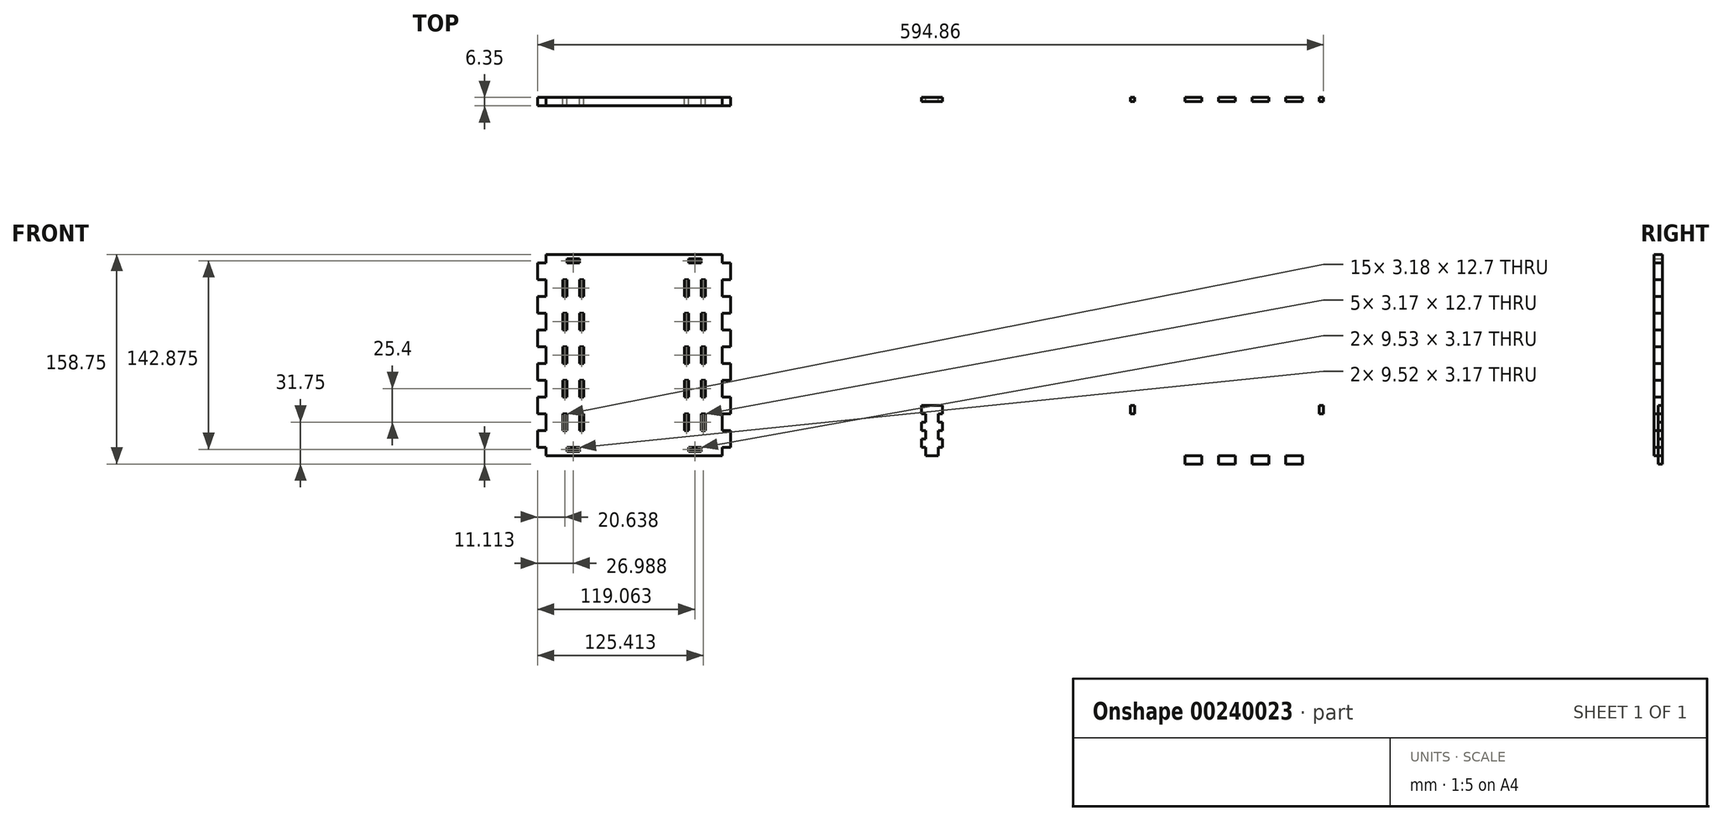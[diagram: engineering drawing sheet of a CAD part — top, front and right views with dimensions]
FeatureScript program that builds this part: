
annotation { "Feature Type Name" : "Feature", "Feature Type Description" : "" }
export const myFeature = defineFeature(function(context is Context, id is Id, definition is map)
    precondition{}
    {
        {
            var Q0;
            Q0=qCreatedBy(makeId("Front.planeOp"),FACE);
            var sketch = newSketch(context, id + "F0", { "sketchPlane" : qUnion([Q0])});
            skLineSegment(sketch, "E0.bottom", {"start": v(0, 0) * mm, "end": v(146.05, 0) * mm});
            skLineSegment(sketch, "E0.top", {"start": v(0, 38.1) * mm, "end": v(146.05, 38.1) * mm});
            skLineSegment(sketch, "E0.left", {"start": v(0, 0) * mm, "end": v(0, 38.1) * mm});
            skLineSegment(sketch, "E0.right", {"start": v(146.05, 0) * mm, "end": v(146.05, 38.1) * mm});
            skLineSegment(sketch, "E1.bottom", {"start": v(0, 38.1) * mm, "end": v(3.17, 38.1) * mm});
            skLineSegment(sketch, "E1.top", {"start": v(0, 31.75) * mm, "end": v(3.17, 31.75) * mm});
            skLineSegment(sketch, "E1.left", {"start": v(0, 38.1) * mm, "end": v(0, 31.75) * mm});
            skLineSegment(sketch, "E1.right", {"start": v(3.17, 38.1) * mm, "end": v(3.17, 31.75) * mm});
            skLineSegment(sketch, "E2.0.1.0", {"start": v(0, 19.05) * mm, "end": v(3.17, 19.05) * mm});
            skLineSegment(sketch, "E2.0.1.1", {"start": v(3.17, 25.4) * mm, "end": v(3.17, 19.05) * mm});
            skLineSegment(sketch, "E2.0.1.2", {"start": v(0, 25.4) * mm, "end": v(3.17, 25.4) * mm});
            skLineSegment(sketch, "E2.0.1.3", {"start": v(0, 25.4) * mm, "end": v(0, 19.05) * mm});
            skLineSegment(sketch, "E2.0.2.0", {"start": v(0, 6.35) * mm, "end": v(3.17, 6.35) * mm});
            skLineSegment(sketch, "E2.0.2.1", {"start": v(3.17, 12.7) * mm, "end": v(3.17, 6.35) * mm});
            skLineSegment(sketch, "E2.0.2.2", {"start": v(0, 12.7) * mm, "end": v(3.17, 12.7) * mm});
            skLineSegment(sketch, "E2.0.2.3", {"start": v(0, 12.7) * mm, "end": v(0, 6.35) * mm});
            skLineSegment(sketch, "E2.direction1", {"start": v(0, 25.4) * mm, "end": v(25.4, 25.4) * mm, "construction": true});
            skLineSegment(sketch, "E2.direction2", {"start": v(0, 25.4) * mm, "end": v(0, 12.7) * mm, "construction": true});
            skLineSegment(sketch, "E3.bottom", {"start": v(15.88, 0) * mm, "end": v(28.58, 0) * mm});
            skLineSegment(sketch, "E3.top", {"start": v(15.88, -6.35) * mm, "end": v(28.58, -6.35) * mm});
            skLineSegment(sketch, "E3.left", {"start": v(15.88, 0) * mm, "end": v(15.88, -6.35) * mm});
            skLineSegment(sketch, "E3.right", {"start": v(28.58, 0) * mm, "end": v(28.58, -6.35) * mm});
            skLineSegment(sketch, "E4.1.0.0", {"start": v(41.27, -6.35) * mm, "end": v(53.97, -6.35) * mm});
            skLineSegment(sketch, "E4.1.0.1", {"start": v(53.97, 0) * mm, "end": v(53.97, -6.35) * mm});
            skLineSegment(sketch, "E4.1.0.2", {"start": v(41.27, 0) * mm, "end": v(41.27, -6.35) * mm});
            skLineSegment(sketch, "E4.1.0.3", {"start": v(41.27, 0) * mm, "end": v(53.97, 0) * mm});
            skLineSegment(sketch, "E4.2.0.0", {"start": v(66.67, -6.35) * mm, "end": v(79.37, -6.35) * mm});
            skLineSegment(sketch, "E4.2.0.1", {"start": v(79.37, 0) * mm, "end": v(79.37, -6.35) * mm});
            skLineSegment(sketch, "E4.2.0.2", {"start": v(66.67, 0) * mm, "end": v(66.67, -6.35) * mm});
            skLineSegment(sketch, "E4.2.0.3", {"start": v(66.67, 0) * mm, "end": v(79.37, 0) * mm});
            skLineSegment(sketch, "E4.3.0.0", {"start": v(92.07, -6.35) * mm, "end": v(104.77, -6.35) * mm});
            skLineSegment(sketch, "E4.3.0.1", {"start": v(104.77, 0) * mm, "end": v(104.77, -6.35) * mm});
            skLineSegment(sketch, "E4.3.0.2", {"start": v(92.07, 0) * mm, "end": v(92.07, -6.35) * mm});
            skLineSegment(sketch, "E4.3.0.3", {"start": v(92.07, 0) * mm, "end": v(104.77, 0) * mm});
            skLineSegment(sketch, "E4.4.0.0", {"start": v(117.47, -6.35) * mm, "end": v(130.17, -6.35) * mm});
            skLineSegment(sketch, "E4.4.0.1", {"start": v(130.17, 0) * mm, "end": v(130.17, -6.35) * mm});
            skLineSegment(sketch, "E4.4.0.2", {"start": v(117.47, 0) * mm, "end": v(117.47, -6.35) * mm});
            skLineSegment(sketch, "E4.4.0.3", {"start": v(117.47, 0) * mm, "end": v(130.17, 0) * mm});
            skLineSegment(sketch, "E4.direction1", {"start": v(3.18, -3.18) * mm, "end": v(28.58, -3.18) * mm, "construction": true});
            skLineSegment(sketch, "E5", {"start": v(73.03, 38.1) * mm, "end": v(73.03, 0) * mm, "construction": true});
            skLineSegment(sketch, "E6.MirrorCS", {"start": v(146.05, 12.7) * mm, "end": v(142.88, 12.7) * mm});
            skLineSegment(sketch, "E7.MirrorCS", {"start": v(146.05, 31.75) * mm, "end": v(142.88, 31.75) * mm});
            skLineSegment(sketch, "E8.MirrorCS", {"start": v(146.05, 19.05) * mm, "end": v(142.88, 19.05) * mm});
            skLineSegment(sketch, "E9.MirrorCS", {"start": v(146.05, 25.4) * mm, "end": v(142.88, 25.4) * mm});
            skLineSegment(sketch, "E10.MirrorCS", {"start": v(146.05, 6.35) * mm, "end": v(142.88, 6.35) * mm});
            skLineSegment(sketch, "E11.MirrorCS", {"start": v(142.88, 12.7) * mm, "end": v(142.88, 6.35) * mm});
            skLineSegment(sketch, "E12.MirrorCS", {"start": v(142.88, 38.1) * mm, "end": v(142.88, 31.75) * mm});
            skLineSegment(sketch, "E13.MirrorCS", {"start": v(142.88, 25.4) * mm, "end": v(142.88, 19.05) * mm});
            skLineSegment(sketch, "E14.MirrorCS", {"start": v(146.05, 25.4) * mm, "end": v(120.65, 25.4) * mm, "construction": true});
            skLineSegment(sketch, "E15.MirrorCS", {"start": v(146.05, 38.1) * mm, "end": v(142.88, 38.1) * mm});
            skLineSegment(sketch, "E16.MirrorCS", {"start": v(146.05, 38.1) * mm, "end": v(146.05, 31.75) * mm});
            skLineSegment(sketch, "E17.MirrorCS", {"start": v(146.05, 25.4) * mm, "end": v(146.05, 12.7) * mm, "construction": true});
            skSolve(sketch);
        }
        {
            var Q0;
            Q0=makeQuery(id+"F0.imprint","IMPRINT",FACE,{"disambiguationData":[TD([[makeQuery(id+"F0.imprint","IMPRINT",EDGE,{"derivedFrom":sQuery(id+"F0.wireOp",EDGE,"E0.top")}),-1.0]])]});
            var Q1;
            Q1=makeQuery(id+"F0.imprint","IMPRINT",FACE,{"disambiguationData":[TD([[makeQuery(id+"F0.imprint","IMPRINT",EDGE,{"derivedFrom":sQuery(id+"F0.wireOp",EDGE,"E3.bottom")}),-1.0]])]});
            var Q2;
            Q2=makeQuery(id+"F0.imprint","IMPRINT",FACE,{"disambiguationData":[TD([[makeQuery(id+"F0.imprint","IMPRINT",EDGE,{"derivedFrom":sQuery(id+"F0.wireOp",EDGE,"E4.1.0.0")}),1.0]])]});
            var Q3;
            Q3=makeQuery(id+"F0.imprint","IMPRINT",FACE,{"disambiguationData":[TD([[makeQuery(id+"F0.imprint","IMPRINT",EDGE,{"derivedFrom":sQuery(id+"F0.wireOp",EDGE,"E4.2.0.0")}),1.0]])]});
            var Q4;
            Q4=makeQuery(id+"F0.imprint","IMPRINT",FACE,{"disambiguationData":[TD([[makeQuery(id+"F0.imprint","IMPRINT",EDGE,{"derivedFrom":sQuery(id+"F0.wireOp",EDGE,"E4.3.0.0")}),1.0]])]});
            var Q5;
            Q5=makeQuery(id+"F0.imprint","IMPRINT",FACE,{"disambiguationData":[TD([[makeQuery(id+"F0.imprint","IMPRINT",EDGE,{"derivedFrom":sQuery(id+"F0.wireOp",EDGE,"E4.4.0.0")}),1.0]])]});
            extrude(context, id + "F1", {"entities" : qUnion([Q0, Q1, Q2, Q3, Q4, Q5]), "depth" : 3.17 * mm});
        }
        {
            var Q0;
            Q0=qCreatedBy(makeId("Front.planeOp"),FACE);
            var sketch = newSketch(context, id + "F2", { "sketchPlane" : qUnion([Q0])});
            skLineSegment(sketch, "E18.bottom", {"start": v(-145.64, 0) * mm, "end": v(-155.16, 0) * mm});
            skLineSegment(sketch, "E18.top", {"start": v(-145.64, 38.1) * mm, "end": v(-155.16, 38.1) * mm});
            skLineSegment(sketch, "E18.left", {"start": v(-145.64, 0) * mm, "end": v(-145.64, 38.1) * mm});
            skLineSegment(sketch, "E18.right", {"start": v(-155.16, 0) * mm, "end": v(-155.16, 38.1) * mm});
            skLineSegment(sketch, "E19.bottom", {"start": v(-145.64, 38.1) * mm, "end": v(-142.46, 38.1) * mm});
            skLineSegment(sketch, "E19.top", {"start": v(-145.64, 31.75) * mm, "end": v(-142.46, 31.75) * mm});
            skLineSegment(sketch, "E19.left", {"start": v(-145.64, 38.1) * mm, "end": v(-145.64, 31.75) * mm});
            skLineSegment(sketch, "E19.right", {"start": v(-142.46, 38.1) * mm, "end": v(-142.46, 31.75) * mm});
            skLineSegment(sketch, "E20.0.1.0", {"start": v(-142.46, 25.4) * mm, "end": v(-142.46, 19.05) * mm});
            skLineSegment(sketch, "E20.0.1.1", {"start": v(-145.64, 25.4) * mm, "end": v(-142.46, 25.4) * mm});
            skLineSegment(sketch, "E20.0.1.2", {"start": v(-145.64, 19.05) * mm, "end": v(-142.46, 19.05) * mm});
            skLineSegment(sketch, "E20.0.1.3", {"start": v(-155.16, -12.7) * mm, "end": v(-155.16, 25.4) * mm});
            skLineSegment(sketch, "E20.0.2.0", {"start": v(-142.46, 12.7) * mm, "end": v(-142.46, 6.35) * mm});
            skLineSegment(sketch, "E20.0.2.1", {"start": v(-145.64, 12.7) * mm, "end": v(-142.46, 12.7) * mm});
            skLineSegment(sketch, "E20.0.2.2", {"start": v(-145.64, 6.35) * mm, "end": v(-142.46, 6.35) * mm});
            skLineSegment(sketch, "E20.0.2.3", {"start": v(-155.16, -25.4) * mm, "end": v(-155.16, 12.7) * mm});
            skLineSegment(sketch, "E20.direction1", {"start": v(-145.64, 31.75) * mm, "end": v(-122.14, 31.75) * mm, "construction": true});
            skLineSegment(sketch, "E20.direction2", {"start": v(-145.64, 31.75) * mm, "end": v(-145.64, 19.05) * mm, "construction": true});
            skLineSegment(sketch, "E21", {"start": v(-150.4, 38.1) * mm, "end": v(-150.4, 0) * mm, "construction": true});
            skLineSegment(sketch, "E22.MirrorCS", {"start": v(-155.16, 25.4) * mm, "end": v(-158.34, 25.4) * mm});
            skLineSegment(sketch, "E23.MirrorCS", {"start": v(-155.16, 19.05) * mm, "end": v(-158.34, 19.05) * mm});
            skLineSegment(sketch, "E24.MirrorCS", {"start": v(-155.16, 31.75) * mm, "end": v(-158.34, 31.75) * mm});
            skLineSegment(sketch, "E25.MirrorCS", {"start": v(-155.16, 38.1) * mm, "end": v(-158.34, 38.1) * mm});
            skLineSegment(sketch, "E26.MirrorCS", {"start": v(-155.16, 12.7) * mm, "end": v(-158.34, 12.7) * mm});
            skLineSegment(sketch, "E27.MirrorCS", {"start": v(-155.16, 6.35) * mm, "end": v(-158.34, 6.35) * mm});
            skLineSegment(sketch, "E28.MirrorCS", {"start": v(-158.34, 38.1) * mm, "end": v(-158.34, 31.75) * mm});
            skLineSegment(sketch, "E29.MirrorCS", {"start": v(-158.34, 25.4) * mm, "end": v(-158.34, 19.05) * mm});
            skLineSegment(sketch, "E30.MirrorCS", {"start": v(-158.34, 12.7) * mm, "end": v(-158.34, 6.35) * mm});
            skLineSegment(sketch, "E31.MirrorCS", {"start": v(-155.16, 31.75) * mm, "end": v(-178.66, 31.75) * mm, "construction": true});
            skLineSegment(sketch, "E32.bottom", {"start": v(-155.16, 0) * mm, "end": v(-145.64, 0) * mm});
            skLineSegment(sketch, "E32.top", {"start": v(-155.16, -6.35) * mm, "end": v(-145.64, -6.35) * mm});
            skLineSegment(sketch, "E32.left", {"start": v(-155.16, 0) * mm, "end": v(-155.16, -6.35) * mm});
            skLineSegment(sketch, "E32.right", {"start": v(-145.64, 0) * mm, "end": v(-145.64, -6.35) * mm});
            skSolve(sketch);
        }
        {
            var Q0;
            {var subQ7=sQuery(id+"F2.wireOp",EDGE,"E18.top");Q0=makeQuery(id+"F2.imprint","IMPRINT",FACE,{"disambiguationData":[TD([[makeQuery(id+"F2.imprint","IMPRINT",EDGE,{"derivedFrom":subQ7}),1.0]])]});}
            var Q1;
            {var subQ0=sQuery(id+"F2.wireOp",EDGE,"E22.MirrorCS");Q1=makeQuery(id+"F2.imprint","IMPRINT",FACE,{"disambiguationData":[TD([[makeQuery(id+"F2.imprint","IMPRINT",EDGE,{"derivedFrom":subQ0}),1.0]])]});}
            var Q2;
            {var subQ0=sQuery(id+"F2.wireOp",EDGE,"E26.MirrorCS");Q2=makeQuery(id+"F2.imprint","IMPRINT",FACE,{"disambiguationData":[TD([[makeQuery(id+"F2.imprint","IMPRINT",EDGE,{"derivedFrom":subQ0}),1.0]])]});}
            var Q3;
            Q3=makeQuery(id+"F2.imprint","IMPRINT",FACE,{"disambiguationData":[TD([[makeQuery(id+"F2.imprint","IMPRINT",EDGE,{"derivedFrom":sQuery(id+"F2.wireOp",EDGE,"E20.0.2.0")}),-1.0]])]});
            var Q4;
            Q4=makeQuery(id+"F2.imprint","IMPRINT",FACE,{"disambiguationData":[TD([[makeQuery(id+"F2.imprint","IMPRINT",EDGE,{"derivedFrom":sQuery(id+"F2.wireOp",EDGE,"E20.0.1.0")}),-1.0]])]});
            var Q5;
            Q5=makeQuery(id+"F2.imprint","IMPRINT",FACE,{"disambiguationData":[TD([[makeQuery(id+"F2.imprint","IMPRINT",EDGE,{"derivedFrom":sQuery(id+"F2.wireOp",EDGE,"E19.bottom")}),-1.0]])]});
            var Q6;
            {var subQ2=sQuery(id+"F2.wireOp",EDGE,"E24.MirrorCS");Q6=makeQuery(id+"F2.imprint","IMPRINT",FACE,{"disambiguationData":[TD([[makeQuery(id+"F2.imprint","IMPRINT",EDGE,{"derivedFrom":subQ2}),-1.0]])]});}
            var Q7;
            Q7=makeQuery(id+"F2.imprint","IMPRINT",FACE,{"disambiguationData":[TD([[makeQuery(id+"F2.imprint","IMPRINT",EDGE,{"derivedFrom":sQuery(id+"F2.wireOp",EDGE,"E32.bottom")}),-1.0]])]});
            extrude(context, id + "F3", {"entities" : qUnion([Q0, Q1, Q2, Q3, Q4, Q5, Q6, Q7]), "depth" : 3.17 * mm});
        }
        {
            var Q0;
            Q0=qCreatedBy(makeId("Front.planeOp"),FACE);
            var sketch = newSketch(context, id + "F4", { "sketchPlane" : qUnion([Q0])});
            skLineSegment(sketch, "E33.bottom", {"start": v(-309.1, 0) * mm, "end": v(-442.46, 0) * mm});
            skLineSegment(sketch, "E33.top", {"start": v(-309.1, 152.4) * mm, "end": v(-442.46, 152.4) * mm});
            skLineSegment(sketch, "E33.left", {"start": v(-309.1, 0) * mm, "end": v(-309.1, 152.4) * mm});
            skLineSegment(sketch, "E33.right", {"start": v(-442.46, 0) * mm, "end": v(-442.46, 152.4) * mm});
            skLineSegment(sketch, "E34.bottom", {"start": v(-309.1, 146.05) * mm, "end": v(-302.76, 146.05) * mm});
            skLineSegment(sketch, "E34.top", {"start": v(-309.1, 133.35) * mm, "end": v(-302.76, 133.35) * mm});
            skLineSegment(sketch, "E34.left", {"start": v(-309.1, 146.05) * mm, "end": v(-309.1, 133.35) * mm});
            skLineSegment(sketch, "E34.right", {"start": v(-302.76, 146.05) * mm, "end": v(-302.76, 133.35) * mm});
            skLineSegment(sketch, "E35.0.1.0", {"start": v(-309.1, 107.95) * mm, "end": v(-302.76, 107.95) * mm});
            skLineSegment(sketch, "E35.0.1.1", {"start": v(-309.1, 120.65) * mm, "end": v(-302.76, 120.65) * mm});
            skLineSegment(sketch, "E35.0.1.2", {"start": v(-302.76, 120.65) * mm, "end": v(-302.76, 107.95) * mm});
            skLineSegment(sketch, "E35.0.2.0", {"start": v(-309.1, 82.55) * mm, "end": v(-302.76, 82.55) * mm});
            skLineSegment(sketch, "E35.0.2.1", {"start": v(-309.1, 95.25) * mm, "end": v(-302.76, 95.25) * mm});
            skLineSegment(sketch, "E35.0.2.2", {"start": v(-302.76, 95.25) * mm, "end": v(-302.76, 82.55) * mm});
            skLineSegment(sketch, "E35.0.3.0", {"start": v(-309.1, 57.15) * mm, "end": v(-302.76, 57.15) * mm});
            skLineSegment(sketch, "E35.0.3.1", {"start": v(-309.1, 69.85) * mm, "end": v(-302.76, 69.85) * mm});
            skLineSegment(sketch, "E35.0.3.2", {"start": v(-302.76, 69.85) * mm, "end": v(-302.76, 57.15) * mm});
            skLineSegment(sketch, "E35.0.4.0", {"start": v(-309.1, 31.75) * mm, "end": v(-302.76, 31.75) * mm});
            skLineSegment(sketch, "E35.0.4.1", {"start": v(-309.1, 44.45) * mm, "end": v(-302.76, 44.45) * mm});
            skLineSegment(sketch, "E35.0.4.2", {"start": v(-302.76, 44.45) * mm, "end": v(-302.76, 31.75) * mm});
            skLineSegment(sketch, "E35.0.5.0", {"start": v(-309.1, 6.35) * mm, "end": v(-302.76, 6.35) * mm});
            skLineSegment(sketch, "E35.0.5.1", {"start": v(-309.1, 19.05) * mm, "end": v(-302.76, 19.05) * mm});
            skLineSegment(sketch, "E35.0.5.2", {"start": v(-302.76, 19.05) * mm, "end": v(-302.76, 6.35) * mm});
            skLineSegment(sketch, "E35.direction1", {"start": v(-309.1, 133.35) * mm, "end": v(-283.7, 133.35) * mm, "construction": true});
            skLineSegment(sketch, "E35.direction2", {"start": v(-309.1, 133.35) * mm, "end": v(-309.1, 107.95) * mm, "construction": true});
            skLineSegment(sketch, "E36", {"start": v(-375.78, 152.4) * mm, "end": v(-375.78, 0) * mm, "construction": true});
            skLineSegment(sketch, "E37.MirrorCS", {"start": v(-442.46, 31.75) * mm, "end": v(-448.8, 31.75) * mm});
            skLineSegment(sketch, "E38.MirrorCS", {"start": v(-442.46, 57.15) * mm, "end": v(-448.8, 57.15) * mm});
            skLineSegment(sketch, "E39.MirrorCS", {"start": v(-442.46, 69.85) * mm, "end": v(-448.8, 69.85) * mm});
            skLineSegment(sketch, "E40.MirrorCS", {"start": v(-442.46, 146.05) * mm, "end": v(-448.8, 146.05) * mm});
            skLineSegment(sketch, "E41.MirrorCS", {"start": v(-442.46, 133.35) * mm, "end": v(-448.8, 133.35) * mm});
            skLineSegment(sketch, "E42.MirrorCS", {"start": v(-442.46, 107.95) * mm, "end": v(-448.8, 107.95) * mm});
            skLineSegment(sketch, "E43.MirrorCS", {"start": v(-442.46, 120.65) * mm, "end": v(-448.8, 120.65) * mm});
            skLineSegment(sketch, "E44.MirrorCS", {"start": v(-442.46, 6.35) * mm, "end": v(-448.8, 6.35) * mm});
            skLineSegment(sketch, "E45.MirrorCS", {"start": v(-442.46, 19.05) * mm, "end": v(-448.8, 19.05) * mm});
            skLineSegment(sketch, "E46.MirrorCS", {"start": v(-442.46, 82.55) * mm, "end": v(-448.8, 82.55) * mm});
            skLineSegment(sketch, "E47.MirrorCS", {"start": v(-442.46, 44.45) * mm, "end": v(-448.8, 44.45) * mm});
            skLineSegment(sketch, "E48.MirrorCS", {"start": v(-442.46, 95.25) * mm, "end": v(-448.8, 95.25) * mm});
            skLineSegment(sketch, "E49.MirrorCS", {"start": v(-448.8, 95.25) * mm, "end": v(-448.8, 82.55) * mm});
            skLineSegment(sketch, "E50.MirrorCS", {"start": v(-448.8, 69.85) * mm, "end": v(-448.8, 57.15) * mm});
            skLineSegment(sketch, "E51.MirrorCS", {"start": v(-442.46, 133.35) * mm, "end": v(-467.86, 133.35) * mm, "construction": true});
            skLineSegment(sketch, "E52.MirrorCS", {"start": v(-448.8, 146.05) * mm, "end": v(-448.8, 133.35) * mm});
            skLineSegment(sketch, "E53.MirrorCS", {"start": v(-448.8, 19.05) * mm, "end": v(-448.8, 6.35) * mm});
            skLineSegment(sketch, "E54.MirrorCS", {"start": v(-448.8, 120.65) * mm, "end": v(-448.8, 107.95) * mm});
            skLineSegment(sketch, "E55.MirrorCS", {"start": v(-448.8, 44.45) * mm, "end": v(-448.8, 31.75) * mm});
            skLineSegment(sketch, "E56.bottom", {"start": v(-429.76, 133.35) * mm, "end": v(-426.58, 133.35) * mm});
            skLineSegment(sketch, "E56.top", {"start": v(-429.76, 120.65) * mm, "end": v(-426.58, 120.65) * mm});
            skLineSegment(sketch, "E56.left", {"start": v(-429.76, 133.35) * mm, "end": v(-429.76, 120.65) * mm});
            skLineSegment(sketch, "E56.right", {"start": v(-426.58, 133.35) * mm, "end": v(-426.58, 120.65) * mm});
            skLineSegment(sketch, "E57.0.1.0", {"start": v(-426.58, 107.95) * mm, "end": v(-426.58, 95.25) * mm});
            skLineSegment(sketch, "E57.0.1.1", {"start": v(-429.76, 107.95) * mm, "end": v(-429.76, 95.25) * mm});
            skLineSegment(sketch, "E57.0.1.2", {"start": v(-429.76, 107.95) * mm, "end": v(-426.58, 107.95) * mm});
            skLineSegment(sketch, "E57.0.1.3", {"start": v(-429.76, 95.25) * mm, "end": v(-426.58, 95.25) * mm});
            skLineSegment(sketch, "E57.0.1.4", {"start": v(-442.46, -25.4) * mm, "end": v(-442.46, 127) * mm});
            skLineSegment(sketch, "E57.0.2.0", {"start": v(-426.58, 82.55) * mm, "end": v(-426.58, 69.85) * mm});
            skLineSegment(sketch, "E57.0.2.1", {"start": v(-429.76, 82.55) * mm, "end": v(-429.76, 69.85) * mm});
            skLineSegment(sketch, "E57.0.2.2", {"start": v(-429.76, 82.55) * mm, "end": v(-426.58, 82.55) * mm});
            skLineSegment(sketch, "E57.0.2.3", {"start": v(-429.76, 69.85) * mm, "end": v(-426.58, 69.85) * mm});
            skLineSegment(sketch, "E57.0.2.4", {"start": v(-442.46, -50.8) * mm, "end": v(-442.46, 101.6) * mm});
            skLineSegment(sketch, "E57.0.3.0", {"start": v(-426.58, 57.15) * mm, "end": v(-426.58, 44.45) * mm});
            skLineSegment(sketch, "E57.0.3.1", {"start": v(-429.76, 57.15) * mm, "end": v(-429.76, 44.45) * mm});
            skLineSegment(sketch, "E57.0.3.2", {"start": v(-429.76, 57.15) * mm, "end": v(-426.58, 57.15) * mm});
            skLineSegment(sketch, "E57.0.3.3", {"start": v(-429.76, 44.45) * mm, "end": v(-426.58, 44.45) * mm});
            skLineSegment(sketch, "E57.0.3.4", {"start": v(-442.46, -76.2) * mm, "end": v(-442.46, 76.2) * mm});
            skLineSegment(sketch, "E57.0.4.0", {"start": v(-426.58, 31.75) * mm, "end": v(-426.58, 19.05) * mm});
            skLineSegment(sketch, "E57.0.4.1", {"start": v(-429.76, 31.75) * mm, "end": v(-429.76, 19.05) * mm});
            skLineSegment(sketch, "E57.0.4.2", {"start": v(-429.76, 31.75) * mm, "end": v(-426.58, 31.75) * mm});
            skLineSegment(sketch, "E57.0.4.3", {"start": v(-429.76, 19.05) * mm, "end": v(-426.58, 19.05) * mm});
            skLineSegment(sketch, "E57.0.4.4", {"start": v(-442.46, -101.6) * mm, "end": v(-442.46, 50.8) * mm});
            skLineSegment(sketch, "E57.direction1", {"start": v(-429.76, 120.65) * mm, "end": v(-404.36, 120.65) * mm, "construction": true});
            skLineSegment(sketch, "E57.direction2", {"start": v(-429.76, 120.65) * mm, "end": v(-429.76, 95.25) * mm, "construction": true});
            skLineSegment(sketch, "E58", {"start": v(-421.82, 152.4) * mm, "end": v(-421.82, 0) * mm, "construction": true});
            skLineSegment(sketch, "E59.MirrorCS", {"start": v(-413.88, 107.95) * mm, "end": v(-413.88, 95.25) * mm});
            skLineSegment(sketch, "E60.MirrorCS", {"start": v(-413.88, 133.35) * mm, "end": v(-413.88, 120.65) * mm});
            skLineSegment(sketch, "E61.MirrorCS", {"start": v(-417.06, 133.35) * mm, "end": v(-417.06, 120.65) * mm});
            skLineSegment(sketch, "E62.MirrorCS", {"start": v(-413.88, 82.55) * mm, "end": v(-413.88, 69.85) * mm});
            skLineSegment(sketch, "E63.MirrorCS", {"start": v(-413.88, 82.55) * mm, "end": v(-417.06, 82.55) * mm});
            skLineSegment(sketch, "E64.MirrorCS", {"start": v(-417.06, 107.95) * mm, "end": v(-417.06, 95.25) * mm});
            skLineSegment(sketch, "E65.MirrorCS", {"start": v(-413.88, 69.85) * mm, "end": v(-417.06, 69.85) * mm});
            skLineSegment(sketch, "E66.MirrorCS", {"start": v(-413.88, 95.25) * mm, "end": v(-417.06, 95.25) * mm});
            skLineSegment(sketch, "E67.MirrorCS", {"start": v(-417.06, 57.15) * mm, "end": v(-417.06, 44.45) * mm});
            skLineSegment(sketch, "E68.MirrorCS", {"start": v(-413.88, 133.35) * mm, "end": v(-417.06, 133.35) * mm});
            skLineSegment(sketch, "E69.MirrorCS", {"start": v(-417.06, 82.55) * mm, "end": v(-417.06, 69.85) * mm});
            skLineSegment(sketch, "E70.MirrorCS", {"start": v(-413.88, 120.65) * mm, "end": v(-417.06, 120.65) * mm});
            skLineSegment(sketch, "E71.MirrorCS", {"start": v(-413.88, 57.15) * mm, "end": v(-417.06, 57.15) * mm});
            skLineSegment(sketch, "E72.MirrorCS", {"start": v(-413.88, 120.65) * mm, "end": v(-413.88, 95.25) * mm, "construction": true});
            skLineSegment(sketch, "E73.MirrorCS", {"start": v(-413.88, 107.95) * mm, "end": v(-417.06, 107.95) * mm});
            skLineSegment(sketch, "E74.MirrorCS", {"start": v(-413.88, 44.45) * mm, "end": v(-417.06, 44.45) * mm});
            skLineSegment(sketch, "E75.MirrorCS", {"start": v(-413.88, 57.15) * mm, "end": v(-413.88, 44.45) * mm});
            skLineSegment(sketch, "E76.MirrorCS", {"start": v(-413.88, 19.05) * mm, "end": v(-417.06, 19.05) * mm});
            skLineSegment(sketch, "E77.MirrorCS", {"start": v(-413.88, 31.75) * mm, "end": v(-417.06, 31.75) * mm});
            skLineSegment(sketch, "E78.MirrorCS", {"start": v(-413.88, 31.75) * mm, "end": v(-413.88, 19.05) * mm});
            skLineSegment(sketch, "E79.MirrorCS", {"start": v(-417.06, 31.75) * mm, "end": v(-417.06, 19.05) * mm});
            skLineSegment(sketch, "E80.MirrorCS", {"start": v(-337.68, 120.65) * mm, "end": v(-334.5, 120.65) * mm});
            skLineSegment(sketch, "E81.MirrorCS", {"start": v(-337.68, 95.25) * mm, "end": v(-334.5, 95.25) * mm});
            skLineSegment(sketch, "E82.MirrorCS", {"start": v(-321.8, 133.35) * mm, "end": v(-324.98, 133.35) * mm});
            skLineSegment(sketch, "E83.MirrorCS", {"start": v(-321.8, 95.25) * mm, "end": v(-324.98, 95.25) * mm});
            skLineSegment(sketch, "E84.MirrorCS", {"start": v(-321.8, 107.95) * mm, "end": v(-324.98, 107.95) * mm});
            skLineSegment(sketch, "E85.MirrorCS", {"start": v(-337.68, 57.15) * mm, "end": v(-334.5, 57.15) * mm});
            skLineSegment(sketch, "E86.MirrorCS", {"start": v(-321.8, 120.65) * mm, "end": v(-324.98, 120.65) * mm});
            skLineSegment(sketch, "E87.MirrorCS", {"start": v(-337.68, 31.75) * mm, "end": v(-334.5, 31.75) * mm});
            skLineSegment(sketch, "E88.MirrorCS", {"start": v(-337.68, 19.05) * mm, "end": v(-334.5, 19.05) * mm});
            skLineSegment(sketch, "E89.MirrorCS", {"start": v(-321.8, 44.45) * mm, "end": v(-324.98, 44.45) * mm});
            skLineSegment(sketch, "E90.MirrorCS", {"start": v(-321.8, 57.15) * mm, "end": v(-324.98, 57.15) * mm});
            skLineSegment(sketch, "E91.MirrorCS", {"start": v(-337.68, 82.55) * mm, "end": v(-334.5, 82.55) * mm});
            skLineSegment(sketch, "E92.MirrorCS", {"start": v(-321.8, 31.75) * mm, "end": v(-324.98, 31.75) * mm});
            skLineSegment(sketch, "E93.MirrorCS", {"start": v(-337.68, 44.45) * mm, "end": v(-334.5, 44.45) * mm});
            skLineSegment(sketch, "E94.MirrorCS", {"start": v(-321.8, 82.55) * mm, "end": v(-324.98, 82.55) * mm});
            skLineSegment(sketch, "E95.MirrorCS", {"start": v(-337.68, 107.95) * mm, "end": v(-334.5, 107.95) * mm});
            skLineSegment(sketch, "E96.MirrorCS", {"start": v(-321.8, 19.05) * mm, "end": v(-324.98, 19.05) * mm});
            skLineSegment(sketch, "E97.MirrorCS", {"start": v(-321.8, 69.85) * mm, "end": v(-324.98, 69.85) * mm});
            skLineSegment(sketch, "E98.MirrorCS", {"start": v(-337.68, 133.35) * mm, "end": v(-334.5, 133.35) * mm});
            skLineSegment(sketch, "E99.MirrorCS", {"start": v(-337.68, 69.85) * mm, "end": v(-334.5, 69.85) * mm});
            skLineSegment(sketch, "E100.MirrorCS", {"start": v(-337.68, 107.95) * mm, "end": v(-337.68, 95.25) * mm});
            skLineSegment(sketch, "E101.MirrorCS", {"start": v(-321.8, 107.95) * mm, "end": v(-321.8, 95.25) * mm});
            skLineSegment(sketch, "E102.MirrorCS", {"start": v(-337.68, 82.55) * mm, "end": v(-337.68, 69.85) * mm});
            skLineSegment(sketch, "E103.MirrorCS", {"start": v(-324.98, 57.15) * mm, "end": v(-324.98, 44.45) * mm});
            skLineSegment(sketch, "E104.MirrorCS", {"start": v(-321.8, 57.15) * mm, "end": v(-321.8, 44.45) * mm});
            skLineSegment(sketch, "E105.MirrorCS", {"start": v(-321.8, 31.75) * mm, "end": v(-321.8, 19.05) * mm});
            skLineSegment(sketch, "E106.MirrorCS", {"start": v(-329.75, 152.4) * mm, "end": v(-329.75, 0) * mm, "construction": true});
            skLineSegment(sketch, "E107.MirrorCS", {"start": v(-337.68, 120.65) * mm, "end": v(-337.68, 95.25) * mm, "construction": true});
            skLineSegment(sketch, "E108.MirrorCS", {"start": v(-324.98, 107.95) * mm, "end": v(-324.98, 95.25) * mm});
            skLineSegment(sketch, "E109.MirrorCS", {"start": v(-321.8, 120.65) * mm, "end": v(-347.2, 120.65) * mm, "construction": true});
            skLineSegment(sketch, "E110.MirrorCS", {"start": v(-337.68, 31.75) * mm, "end": v(-337.68, 19.05) * mm});
            skLineSegment(sketch, "E111.MirrorCS", {"start": v(-337.68, 133.35) * mm, "end": v(-337.68, 120.65) * mm});
            skLineSegment(sketch, "E112.MirrorCS", {"start": v(-334.5, 82.55) * mm, "end": v(-334.5, 69.85) * mm});
            skLineSegment(sketch, "E113.MirrorCS", {"start": v(-334.5, 133.35) * mm, "end": v(-334.5, 120.65) * mm});
            skLineSegment(sketch, "E114.MirrorCS", {"start": v(-324.98, 133.35) * mm, "end": v(-324.98, 120.65) * mm});
            skLineSegment(sketch, "E115.MirrorCS", {"start": v(-337.68, 57.15) * mm, "end": v(-337.68, 44.45) * mm});
            skLineSegment(sketch, "E116.MirrorCS", {"start": v(-334.5, 57.15) * mm, "end": v(-334.5, 44.45) * mm});
            skLineSegment(sketch, "E117.MirrorCS", {"start": v(-321.8, 82.55) * mm, "end": v(-321.8, 69.85) * mm});
            skLineSegment(sketch, "E118.MirrorCS", {"start": v(-334.5, 31.75) * mm, "end": v(-334.5, 19.05) * mm});
            skLineSegment(sketch, "E119.MirrorCS", {"start": v(-321.8, 133.35) * mm, "end": v(-321.8, 120.65) * mm});
            skLineSegment(sketch, "E120.MirrorCS", {"start": v(-324.98, 82.55) * mm, "end": v(-324.98, 69.85) * mm});
            skLineSegment(sketch, "E121.MirrorCS", {"start": v(-324.98, 31.75) * mm, "end": v(-324.98, 19.05) * mm});
            skLineSegment(sketch, "E122.MirrorCS", {"start": v(-321.8, 120.65) * mm, "end": v(-321.8, 95.25) * mm, "construction": true});
            skLineSegment(sketch, "E123.MirrorCS", {"start": v(-334.5, 107.95) * mm, "end": v(-334.5, 95.25) * mm});
            skLineSegment(sketch, "E124.bottom", {"start": v(-324.98, 149.23) * mm, "end": v(-334.5, 149.23) * mm});
            skLineSegment(sketch, "E124.top", {"start": v(-324.98, 146.05) * mm, "end": v(-334.5, 146.05) * mm});
            skLineSegment(sketch, "E124.left", {"start": v(-324.98, 149.23) * mm, "end": v(-324.98, 146.05) * mm});
            skLineSegment(sketch, "E124.right", {"start": v(-334.5, 149.23) * mm, "end": v(-334.5, 146.05) * mm});
            skPoint(sketch, "E124.middle", {"position": v(-329.75, 147.64) * mm});
            skLineSegment(sketch, "E125", {"start": v(-309.1, 76.2) * mm, "end": v(-479.2, 76.2) * mm, "construction": true});
            skLineSegment(sketch, "E126.MirrorCS", {"start": v(-329.75, 0) * mm, "end": v(-329.75, 152.4) * mm, "construction": true});
            skLineSegment(sketch, "E127.MirrorCS", {"start": v(-324.98, 3.18) * mm, "end": v(-334.5, 3.18) * mm});
            skLineSegment(sketch, "E128.MirrorCS", {"start": v(-324.98, 6.35) * mm, "end": v(-334.5, 6.35) * mm});
            skLineSegment(sketch, "E129.MirrorCS", {"start": v(-324.98, 3.18) * mm, "end": v(-324.98, 6.35) * mm});
            skLineSegment(sketch, "E130.MirrorCS", {"start": v(-334.5, 3.18) * mm, "end": v(-334.5, 6.35) * mm});
            skPoint(sketch, "E131.MirrorP", {"position": v(-329.75, 4.76) * mm});
            skLineSegment(sketch, "E132.MirrorCS", {"start": v(-426.58, 149.23) * mm, "end": v(-426.58, 146.05) * mm});
            skLineSegment(sketch, "E133.MirrorCS", {"start": v(-417.06, 149.23) * mm, "end": v(-417.06, 146.05) * mm});
            skLineSegment(sketch, "E134.MirrorCS", {"start": v(-426.58, 146.05) * mm, "end": v(-417.06, 146.05) * mm});
            skLineSegment(sketch, "E135.MirrorCS", {"start": v(-426.58, 149.23) * mm, "end": v(-417.06, 149.23) * mm});
            skPoint(sketch, "E136.MirrorP", {"position": v(-421.82, 147.64) * mm});
            skLineSegment(sketch, "E137.MirrorCS", {"start": v(-421.82, 0) * mm, "end": v(-421.82, 152.4) * mm, "construction": true});
            skLineSegment(sketch, "E138.MirrorCS", {"start": v(-426.58, 3.18) * mm, "end": v(-417.06, 3.18) * mm});
            skLineSegment(sketch, "E139.MirrorCS", {"start": v(-426.58, 3.18) * mm, "end": v(-426.58, 6.35) * mm});
            skLineSegment(sketch, "E140.MirrorCS", {"start": v(-417.06, 3.18) * mm, "end": v(-417.06, 6.35) * mm});
            skLineSegment(sketch, "E141.MirrorCS", {"start": v(-426.58, 6.35) * mm, "end": v(-417.06, 6.35) * mm});
            skPoint(sketch, "E142.MirrorP", {"position": v(-421.82, 4.76) * mm});
            skSolve(sketch);
        }
        {
            var Q0;
            Q0 = qSketchRegion(id + "F4", true);
            extrude(context, id + "F5", {"entities" : qUnion([Q0]), "depth" : 6.35 * mm});
        }
    });
